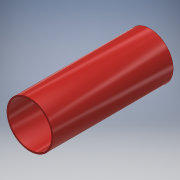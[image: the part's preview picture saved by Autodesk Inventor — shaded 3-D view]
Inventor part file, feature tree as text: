
AUTODESK INVENTOR PART (.ipt)
format: ipt  version: 2018 (Build 220112000, 112)  size: 110,592 bytes
history: native  units: mm
features: other x1, extrude x1, sketch x1
ambient origin geometry x8: Origin, YZ Plane, XZ Plane, XY Plane, X Axis, Y Axis, Z Axis, Center Point
bodies: Body1 (feature_tree)
feature tree (3):
  other  "ソリッド1"
  extrude  "押し出し1"  Depth=90.0mm
  sketch  "スケッチ1"
